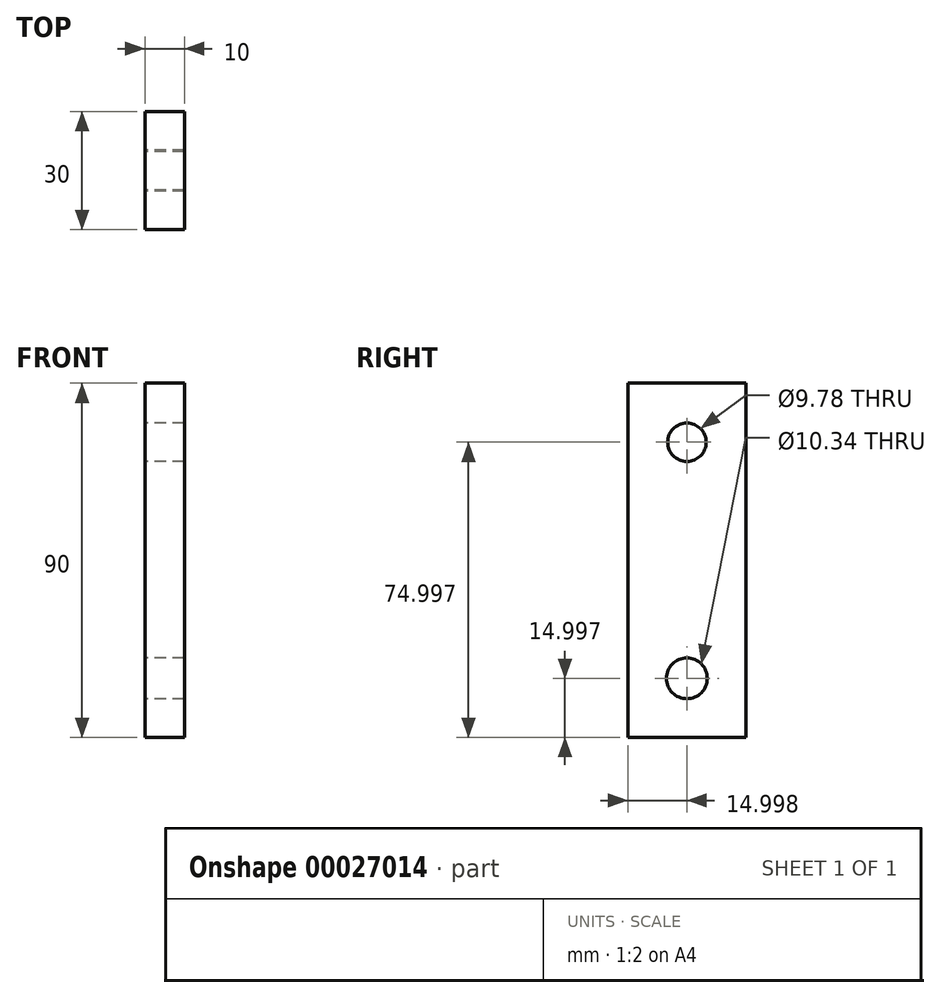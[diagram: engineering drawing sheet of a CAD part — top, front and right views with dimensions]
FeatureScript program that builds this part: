
annotation { "Feature Type Name" : "Feature", "Feature Type Description" : "" }
export const myFeature = defineFeature(function(context is Context, id is Id, definition is map)
    precondition{}
    {
        {
            var Q0;
            Q0=qCreatedBy(makeId("Right.planeOp"),FACE);
            var sketch = newSketch(context, id + "F0", { "sketchPlane" : qUnion([Q0])});
            skLineSegment(sketch, "E0.bottom", {"start": v(-39.35, 44.87) * mm, "end": v(-9.35, 44.87) * mm});
            skLineSegment(sketch, "E0.top", {"start": v(-39.35, -45.13) * mm, "end": v(-9.35, -45.13) * mm});
            skLineSegment(sketch, "E0.left", {"start": v(-39.35, 44.87) * mm, "end": v(-39.35, -45.13) * mm});
            skLineSegment(sketch, "E0.right", {"start": v(-9.35, 44.87) * mm, "end": v(-9.35, -45.13) * mm});
            skCircle(sketch, "E1", {"center": v(-24.35, 29.87) * mm, "radius": 4.89 * mm});
            skCircle(sketch, "E2", {"center": v(-24.35, -30.13) * mm, "radius": 5.17 * mm});
            skSolve(sketch);
        }
        {
            var Q0;
            Q0=makeQuery(id+"F0.imprint","IMPRINT",FACE,{"disambiguationData":[TD([[makeQuery(id+"F0.imprint","IMPRINT",EDGE,{"derivedFrom":sQuery(id+"F0.wireOp",EDGE,"E0.bottom")}),-1.0]])]});
            extrude(context, id + "F1", {"entities" : qUnion([Q0]), "depth" : 10 * mm});
        }
    });
